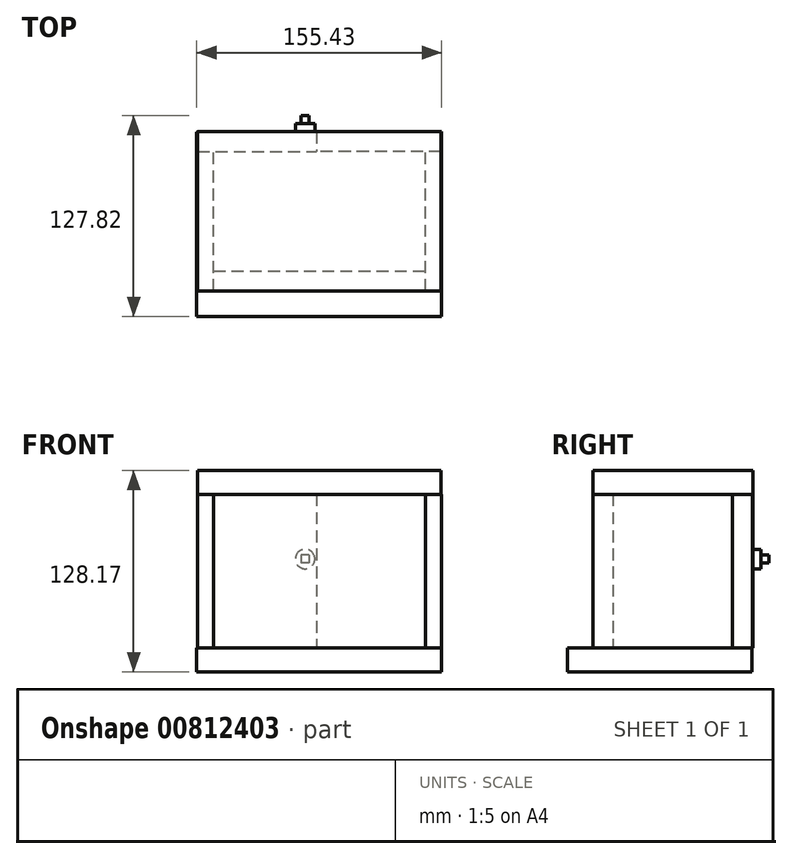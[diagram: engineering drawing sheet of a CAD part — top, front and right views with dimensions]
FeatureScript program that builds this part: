
annotation { "Feature Type Name" : "Feature", "Feature Type Description" : "" }
export const myFeature = defineFeature(function(context is Context, id is Id, definition is map)
    precondition{}
    {
        {
            var Q0;
            Q0=qCreatedBy(makeId("Front.planeOp"),FACE);
            var sketch = newSketch(context, id + "F0", { "sketchPlane" : qUnion([Q0])});
            skLineSegment(sketch, "E0.bottom", {"start": v(-65.36, 48.26) * mm, "end": v(69.07, 48.26) * mm});
            skLineSegment(sketch, "E0.top", {"start": v(-65.36, -49.43) * mm, "end": v(69.07, -49.43) * mm});
            skLineSegment(sketch, "E0.left", {"start": v(-65.36, 48.26) * mm, "end": v(-65.36, -49.43) * mm});
            skLineSegment(sketch, "E0.right", {"start": v(69.07, 48.26) * mm, "end": v(69.07, -49.43) * mm});
            skSolve(sketch);
        }
        {
            var Q0;
            Q0 = qSketchRegion(id + "F0", true);
            extrude(context, id + "F1", {"entities" : qUnion([Q0]), "depth" : 12.7 * mm, "offsetDistance" : 25.4 * mm});
        }
        {
            var Q0;
            Q0=makeQuery(id+"F1.opExtrude","SWEPT_FACE",FACE,{"disambiguationData":[OSD([sQuery(id+"F0.wireOp",EDGE,"E0.right")])]});
            var sketch = newSketch(context, id + "F2", { "sketchPlane" : qUnion([Q0])});
            skLineSegment(sketch, "E1.bottom", {"start": v(-12.7, 48.26) * mm, "end": v(75.71, 48.26) * mm});
            skLineSegment(sketch, "E1.top", {"start": v(-12.7, -49.43) * mm, "end": v(75.71, -49.43) * mm});
            skLineSegment(sketch, "E1.left", {"start": v(-12.7, 48.26) * mm, "end": v(-12.7, -49.43) * mm});
            skLineSegment(sketch, "E1.right", {"start": v(75.71, 48.26) * mm, "end": v(75.71, -49.43) * mm});
            skSolve(sketch);
        }
        {
            var Q0;
            Q0 = qSketchRegion(id + "F2", true);
            extrude(context, id + "F3", {"entities" : qUnion([Q0]), "depth" : 10.16 * mm, "offsetDistance" : 25.4 * mm});
        }
        {
            var Q0;
            Q0=makeQuery(id+"F1.opExtrude","SWEPT_FACE",FACE,{"disambiguationData":[OSD([sQuery(id+"F0.wireOp",EDGE,"E0.left")])]});
            var sketch = newSketch(context, id + "F4", { "sketchPlane" : qUnion([Q0])});
            skLineSegment(sketch, "E2.bottom", {"start": v(12.7, 48.26) * mm, "end": v(-75.9, 48.26) * mm});
            skLineSegment(sketch, "E2.top", {"start": v(12.7, -49.43) * mm, "end": v(-75.9, -49.43) * mm});
            skLineSegment(sketch, "E2.left", {"start": v(12.7, 48.26) * mm, "end": v(12.7, -49.43) * mm});
            skLineSegment(sketch, "E2.right", {"start": v(-75.9, 48.26) * mm, "end": v(-75.9, -49.43) * mm});
            skSolve(sketch);
        }
        {
            var Q0;
            Q0 = qSketchRegion(id + "F4", true);
            extrude(context, id + "F5", {"entities" : qUnion([Q0]), "depth" : 10.16 * mm, "offsetDistance" : 25.4 * mm});
        }
        {
            var Q0;
            Q0=makeQuery(id+"F3.opExtrude","SWEPT_FACE",FACE,{"disambiguationData":[OSD([sQuery(id+"F2.wireOp",EDGE,"E1.right")])]});
            var sketch = newSketch(context, id + "F6", { "sketchPlane" : qUnion([Q0])});
            skLineSegment(sketch, "E3.bottom", {"start": v(-79.23, 48.26) * mm, "end": v(0, 48.26) * mm});
            skLineSegment(sketch, "E3.top", {"start": v(-79.23, -49.43) * mm, "end": v(0, -49.43) * mm});
            skLineSegment(sketch, "E3.left", {"start": v(-79.23, 48.26) * mm, "end": v(-79.23, -49.43) * mm});
            skLineSegment(sketch, "E3.right", {"start": v(0, 48.26) * mm, "end": v(0, -49.43) * mm});
            skSolve(sketch);
        }
        {
            var Q0;
            Q0 = qSketchRegion(id + "F6", true);
            extrude(context, id + "F7", {"entities" : qUnion([Q0]), "depth" : 12.7 * mm, "offsetDistance" : 25.4 * mm});
        }
        {
            var Q0;
            Q0=makeQuery(id+"F5.opExtrude","SWEPT_FACE",FACE,{"disambiguationData":[OSD([sQuery(id+"F4.wireOp",EDGE,"E2.right")])]});
            var sketch = newSketch(context, id + "F8", { "sketchPlane" : qUnion([Q0])});
            skLineSegment(sketch, "E4.bottom", {"start": v(75.52, 48.26) * mm, "end": v(0, 48.26) * mm});
            skLineSegment(sketch, "E4.top", {"start": v(75.52, -49.43) * mm, "end": v(0, -49.43) * mm});
            skLineSegment(sketch, "E4.left", {"start": v(75.52, 48.26) * mm, "end": v(75.52, -49.43) * mm});
            skLineSegment(sketch, "E4.right", {"start": v(0, 48.26) * mm, "end": v(0, -49.43) * mm});
            skSolve(sketch);
        }
        {
            var Q0;
            Q0 = qSketchRegion(id + "F8", true);
            extrude(context, id + "F9", {"entities" : qUnion([Q0]), "depth" : 12.7 * mm, "offsetDistance" : 25.4 * mm});
        }
        {
            var Q0;
            Q0=makeQuery(id+"F9.opExtrude","SWEPT_FACE",FACE,{"disambiguationData":[OSD([sQuery(id+"F8.wireOp",EDGE,"E4.bottom")])]});
            var sketch = newSketch(context, id + "F10", { "sketchPlane" : qUnion([Q0])});
            skLineSegment(sketch, "E5.bottom", {"start": v(-75.52, 88.6) * mm, "end": v(78.95, 88.6) * mm});
            skLineSegment(sketch, "E5.top", {"start": v(-75.52, -12.81) * mm, "end": v(78.95, -12.81) * mm});
            skLineSegment(sketch, "E5.left", {"start": v(-75.52, 88.6) * mm, "end": v(-75.52, -12.81) * mm});
            skLineSegment(sketch, "E5.right", {"start": v(78.95, 88.6) * mm, "end": v(78.95, -12.81) * mm});
            skSolve(sketch);
        }
        {
            var Q0;
            Q0 = qSketchRegion(id + "F10", true);
            extrude(context, id + "F11", {"entities" : qUnion([Q0]), "depth" : 15.24 * mm, "offsetDistance" : 25.4 * mm});
        }
        {
            var Q0;
            Q0=makeQuery(id+"F5.opExtrude","SWEPT_FACE",FACE,{"disambiguationData":[OSD([sQuery(id+"F4.wireOp",EDGE,"E2.top")])]});
            var sketch = newSketch(context, id + "F12", { "sketchPlane" : qUnion([Q0])});
            skLineSegment(sketch, "E6.bottom", {"start": v(-75.52, 12.7) * mm, "end": v(80.23, 12.7) * mm});
            skLineSegment(sketch, "E6.top", {"start": v(-75.52, -88.82) * mm, "end": v(80.23, -88.82) * mm});
            skLineSegment(sketch, "E6.left", {"start": v(-75.52, 12.7) * mm, "end": v(-75.52, -88.82) * mm});
            skLineSegment(sketch, "E6.right", {"start": v(80.23, 12.7) * mm, "end": v(80.23, -88.82) * mm});
            skSolve(sketch);
        }
        {
            var Q0;
            {var subQ1=sQuery(id+"F4.wireOp",EDGE,"E2.top");var subQ2=makeQuery(id+"F5.opExtrude","CAP_EDGE",EDGE,{"disambiguationData":[OSD([subQ1])],"isStart":true});Q0=makeQuery(id+"F12.imprint","IMPRINT",FACE,{"disambiguationData":[TD([[makeQuery(id+"F12.imprint","IMPRINT",EDGE,{"derivedFrom":subQ2}),-1.0]])]});}
            var sketch = newSketch(context, id + "F13", { "sketchPlane" : qUnion([Q0])});
            skLineSegment(sketch, "E7.bottom", {"start": v(-76.11, 29.05) * mm, "end": v(79.32, 29.05) * mm});
            skLineSegment(sketch, "E7.top", {"start": v(-76.11, -88.12) * mm, "end": v(79.32, -88.12) * mm});
            skLineSegment(sketch, "E7.left", {"start": v(-76.11, 29.05) * mm, "end": v(-76.11, -88.12) * mm});
            skLineSegment(sketch, "E7.right", {"start": v(79.32, 29.05) * mm, "end": v(79.32, -88.12) * mm});
            skSolve(sketch);
        }
        {
            var Q0;
            Q0 = qSketchRegion(id + "F13", true);
            extrude(context, id + "F14", {"entities" : qUnion([Q0]), "depth" : 15.24 * mm, "offsetDistance" : 25.4 * mm});
        }
        {
            var Q0;
            Q0=makeQuery(id+"F9.opExtrude","CAP_FACE",FACE,{"disambiguationData":[OSD([sQuery(id+"F8.wireOp",EDGE,"E4.bottom"),sQuery(id+"F8.wireOp",EDGE,"E4.top"),sQuery(id+"F8.wireOp",EDGE,"E4.left"),sQuery(id+"F8.wireOp",EDGE,"E4.right")])],"isStart":false});
            var sketch = newSketch(context, id + "F15", { "sketchPlane" : qUnion([Q0])});
            skCircle(sketch, "E8", {"center": v(7.27, 7.05) * mm, "radius": 6.2 * mm});
            skSolve(sketch);
        }
        {
            var Q0;
            Q0 = qSketchRegion(id + "F15", true);
            extrude(context, id + "F16", {"entities" : qUnion([Q0]), "depth" : 5.08 * mm, "offsetDistance" : 25.4 * mm});
        }
        {
            var Q0;
            Q0=makeQuery(id+"F16.opExtrude","CAP_FACE",FACE,{"disambiguationData":[OSD([sQuery(id+"F15.wireOp",EDGE,"E8")])],"isStart":false});
            var sketch = newSketch(context, id + "F17", { "sketchPlane" : qUnion([Q0])});
            skLineSegment(sketch, "E9.bottom", {"start": v(4.81, 9.78) * mm, "end": v(9.92, 9.78) * mm});
            skLineSegment(sketch, "E9.top", {"start": v(4.81, 4.52) * mm, "end": v(9.92, 4.52) * mm});
            skLineSegment(sketch, "E9.left", {"start": v(4.81, 9.78) * mm, "end": v(4.81, 4.52) * mm});
            skLineSegment(sketch, "E9.right", {"start": v(9.92, 9.78) * mm, "end": v(9.92, 4.52) * mm});
            skSolve(sketch);
        }
        {
            var Q0;
            Q0 = qSketchRegion(id + "F17", true);
            extrude(context, id + "F18", {"entities" : qUnion([Q0]), "depth" : 5.08 * mm, "offsetDistance" : 25.4 * mm});
        }
    });
